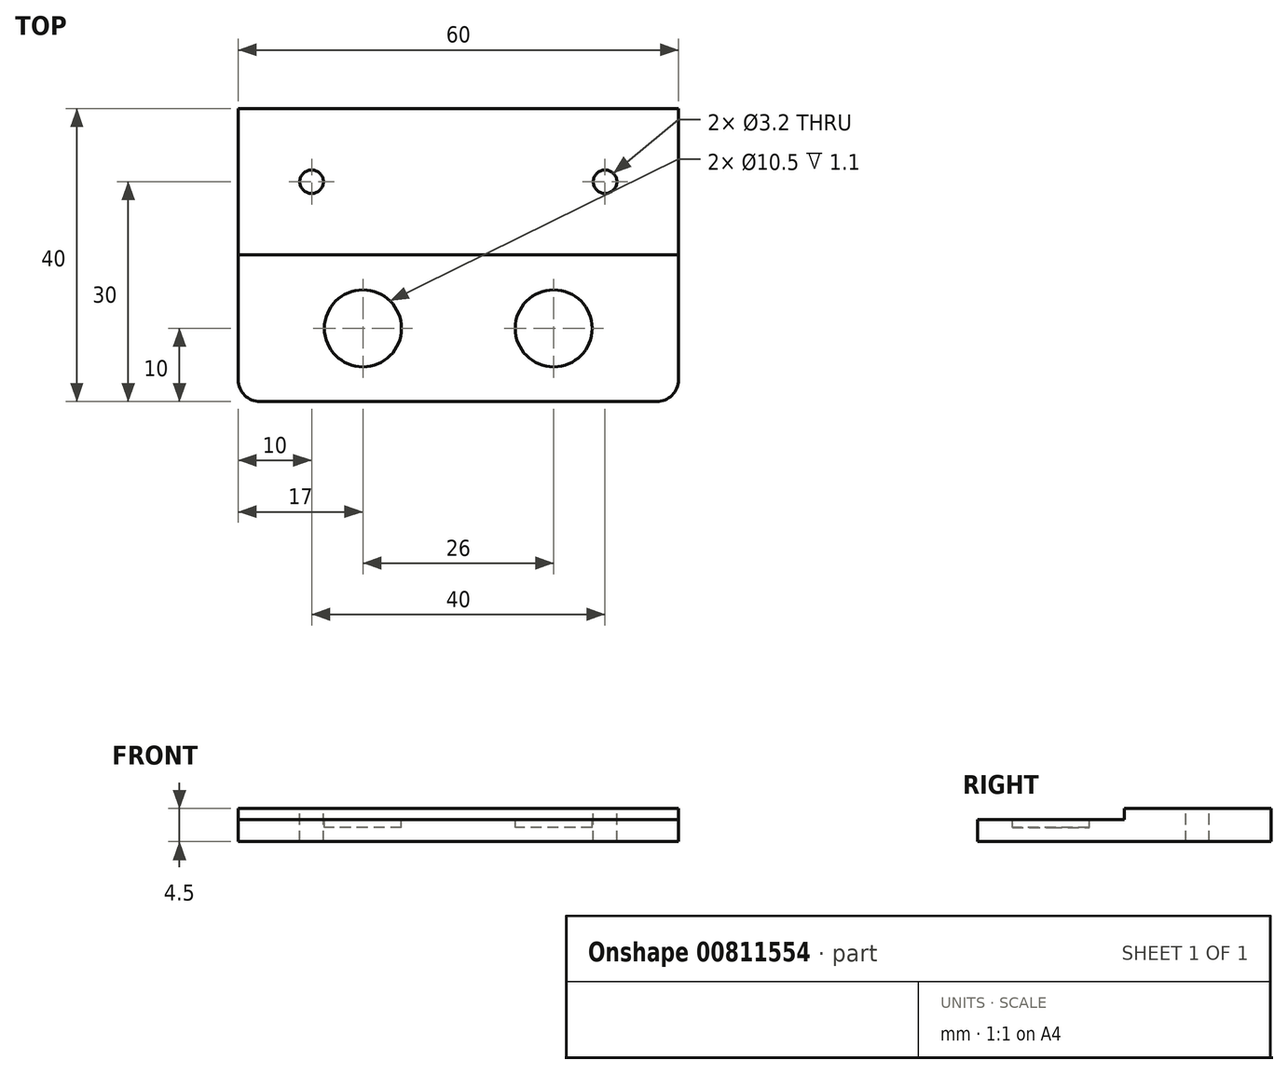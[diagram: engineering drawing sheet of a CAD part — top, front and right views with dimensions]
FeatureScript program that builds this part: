
annotation { "Feature Type Name" : "Feature", "Feature Type Description" : "" }
export const myFeature = defineFeature(function(context is Context, id is Id, definition is map)
    precondition{}
    {
        {
            var Q0;
            Q0=qCreatedBy(makeId("Top.planeOp"),FACE);
            var sketch = newSketch(context, id + "F0", { "sketchPlane" : qUnion([Q0])});
            skLineSegment(sketch, "E0.bottom", {"start": v(30, -20) * mm, "end": v(-30, -20) * mm});
            skLineSegment(sketch, "E0.top", {"start": v(30, 20) * mm, "end": v(-30, 20) * mm});
            skLineSegment(sketch, "E0.left", {"start": v(30, -20) * mm, "end": v(30, 20) * mm});
            skLineSegment(sketch, "E0.right", {"start": v(-30, -20) * mm, "end": v(-30, 20) * mm});
            skPoint(sketch, "E0.middle", {"position": v(0, 0) * mm});
            skSolve(sketch);
        }
        {
            var Q0;
            Q0 = qSketchRegion(id + "F0", true);
            extrude(context, id + "F1", {"entities" : qUnion([Q0]), "depth" : 3 * mm, "offsetDistance" : 25 * mm});
        }
        {
            var Q0;
            Q0=makeQuery(id+"F1.opExtrude","CAP_FACE",FACE,{"disambiguationData":[OSD([sQuery(id+"F0.wireOp",EDGE,"E0.bottom"),sQuery(id+"F0.wireOp",EDGE,"E0.top"),sQuery(id+"F0.wireOp",EDGE,"E0.left"),sQuery(id+"F0.wireOp",EDGE,"E0.right")])],"isStart":false});
            var sketch = newSketch(context, id + "F2", { "sketchPlane" : qUnion([Q0])});
            skLineSegment(sketch, "E1", {"start": v(0, 20) * mm, "end": v(0, -20) * mm, "construction": true});
            skLineSegment(sketch, "E2", {"start": v(-30, 0) * mm, "end": v(30, 0) * mm, "construction": true});
            skPoint(sketch, "E3", {"position": v(-20, 10) * mm});
            skPoint(sketch, "E4", {"position": v(20, 10) * mm});
            skLineSegment(sketch, "E5.bottom", {"start": v(-30, 0) * mm, "end": v(30, 0) * mm});
            skLineSegment(sketch, "E5.top", {"start": v(-30, -20) * mm, "end": v(30, -20) * mm});
            skLineSegment(sketch, "E5.left", {"start": v(-30, 0) * mm, "end": v(-30, -20) * mm});
            skLineSegment(sketch, "E5.right", {"start": v(30, 0) * mm, "end": v(30, -20) * mm});
            skLineSegment(sketch, "E6", {"start": v(-30, -10) * mm, "end": v(30, -10) * mm, "construction": true});
            skLineSegment(sketch, "E7.bottom", {"start": v(-30, 0) * mm, "end": v(0, 0) * mm, "construction": true});
            skLineSegment(sketch, "E7.top", {"start": v(-30, -20) * mm, "end": v(0, -20) * mm, "construction": true});
            skLineSegment(sketch, "E7.left", {"start": v(-30, 0) * mm, "end": v(-30, -20) * mm, "construction": true});
            skLineSegment(sketch, "E7.right", {"start": v(0, 0) * mm, "end": v(0, -20) * mm, "construction": true});
            skLineSegment(sketch, "E8.bottom", {"start": v(0, 0) * mm, "end": v(30, 0) * mm, "construction": true});
            skLineSegment(sketch, "E8.top", {"start": v(0, -20) * mm, "end": v(30, -20) * mm, "construction": true});
            skLineSegment(sketch, "E8.right", {"start": v(30, 0) * mm, "end": v(30, -20) * mm, "construction": true});
            skLineSegment(sketch, "E9", {"start": v(15, 0) * mm, "end": v(15, -20) * mm, "construction": true});
            skCircle(sketch, "E10", {"center": v(-13, -10) * mm, "radius": 5.25 * mm});
            skCircle(sketch, "E11", {"center": v(13, -10) * mm, "radius": 5.25 * mm});
            skLineSegment(sketch, "E12", {"start": v(-15, 0) * mm, "end": v(-15, -20) * mm, "construction": true});
            skLineSegment(sketch, "E13.bottom", {"start": v(-30, 20) * mm, "end": v(0, 20) * mm, "construction": true});
            skLineSegment(sketch, "E13.left", {"start": v(-30, 20) * mm, "end": v(-30, 0) * mm, "construction": true});
            skLineSegment(sketch, "E13.right", {"start": v(0, 20) * mm, "end": v(0, 0) * mm, "construction": true});
            skLineSegment(sketch, "E14.bottom", {"start": v(0, 20) * mm, "end": v(30, 20) * mm, "construction": true});
            skLineSegment(sketch, "E14.right", {"start": v(30, 20) * mm, "end": v(30, 0) * mm, "construction": true});
            skLineSegment(sketch, "E15", {"start": v(-15, 0) * mm, "end": v(-15, 20) * mm, "construction": true});
            skLineSegment(sketch, "E16", {"start": v(-30, 10) * mm, "end": v(0, 10) * mm, "construction": true});
            skLineSegment(sketch, "E17", {"start": v(0, 10) * mm, "end": v(30, 10) * mm, "construction": true});
            skLineSegment(sketch, "E18", {"start": v(15, 0) * mm, "end": v(15, 20) * mm, "construction": true});
            skSolve(sketch);
        }
        {
            var Q0;
            Q0=sQuery(id+"F2.wireOp",VERTEX,"E3");
            var Q1;
            Q1=sQuery(id+"F2.wireOp",VERTEX,"E4");
            var Q2;
            Q2=makeQuery(id+"F1.opExtrude","SWEPT_BODY",BODY,{"disambiguationData":[OSD([sQuery(id+"F0.wireOp",EDGE,"E0.bottom"),sQuery(id+"F0.wireOp",EDGE,"E0.top"),sQuery(id+"F0.wireOp",EDGE,"E0.left"),sQuery(id+"F0.wireOp",EDGE,"E0.right")])]});
            hole(context, id + "F3", {"style" : HoleStyle.SIMPLE, "endStyle" : HoleEndStyle.BLIND, "holeDiameter" : 3.2 * mm, "majorDiameter" : 5 * mm, "holeDepth" : 5 * mm, "isTappedThrough" : true, "tappedDepth" : 12 * mm, "tapClearance" : 3, "locations" : qUnion([Q0, Q1]), "scope" : qUnion([Q2])});
        }
        {
            var Q0;
            Q0=makeQuery(id+"F2.imprint","IMPRINT",FACE,{"disambiguationData":[TD([[makeQuery(id+"F2.imprint","IMPRINT",EDGE,{"derivedFrom":sQuery(id+"F2.wireOp",EDGE,"E10")}),1.0]])]});
            var Q1;
            Q1=makeQuery(id+"F2.imprint","IMPRINT",FACE,{"disambiguationData":[TD([[makeQuery(id+"F2.imprint","IMPRINT",EDGE,{"derivedFrom":sQuery(id+"F2.wireOp",EDGE,"E11")}),1.0]])]});
            extrude(context, id + "F4", {"entities" : qUnion([Q0, Q1]), "operationType" : NewBodyOperationType.REMOVE, "oppositeDirection" : true, "depth" : 1.1 * mm, "offsetDistance" : 25 * mm});
        }
        {
            var Q0;
            Q0=makeQuery(id+"F1.opExtrude","CAP_FACE",FACE,{"disambiguationData":[OSD([sQuery(id+"F0.wireOp",EDGE,"E0.bottom"),sQuery(id+"F0.wireOp",EDGE,"E0.top"),sQuery(id+"F0.wireOp",EDGE,"E0.left"),sQuery(id+"F0.wireOp",EDGE,"E0.right")])],"isStart":false});
            var sketch = newSketch(context, id + "F5", { "sketchPlane" : qUnion([Q0])});
            skLineSegment(sketch, "E19.bottom", {"start": v(-30, 20) * mm, "end": v(30, 20) * mm});
            skLineSegment(sketch, "E19.top", {"start": v(-30, 0) * mm, "end": v(30, 0) * mm});
            skLineSegment(sketch, "E19.left", {"start": v(-30, 20) * mm, "end": v(-30, 0) * mm});
            skLineSegment(sketch, "E19.right", {"start": v(30, 20) * mm, "end": v(30, 0) * mm});
            skSolve(sketch);
        }
        {
            var Q0;
            Q0=makeQuery(id+"F5.imprint","IMPRINT",FACE,{"disambiguationData":[TD([[makeQuery(id+"F5.imprint","IMPRINT",EDGE,{"derivedFrom":sQuery(id+"F5.wireOp",EDGE,"E19.bottom")}),1.0]])]});
            extrude(context, id + "F6", {"entities" : qUnion([Q0]), "operationType" : NewBodyOperationType.ADD, "depth" : 1.5 * mm, "offsetDistance" : 25 * mm});
        }
        {
            var Q0;
            Q0=makeQuery(id+"F1.opExtrude","SWEPT_EDGE",EDGE,{"disambiguationData":[OSD([sQuery(id+"F0.wireOp",EDGE,"E0.bottom"),sQuery(id+"F0.wireOp",EDGE,"E0.left")])]});
            var Q1;
            Q1=makeQuery(id+"F1.opExtrude","SWEPT_EDGE",EDGE,{"disambiguationData":[OSD([sQuery(id+"F0.wireOp",EDGE,"E0.bottom"),sQuery(id+"F0.wireOp",EDGE,"E0.right")])]});
            fillet(context, id + "F7", {"entities" : qUnion([Q0, Q1]), "radius" : 3 * mm, "tangentPropagation" : true, "allowEdgeOverflow" : false});
        }
    });
